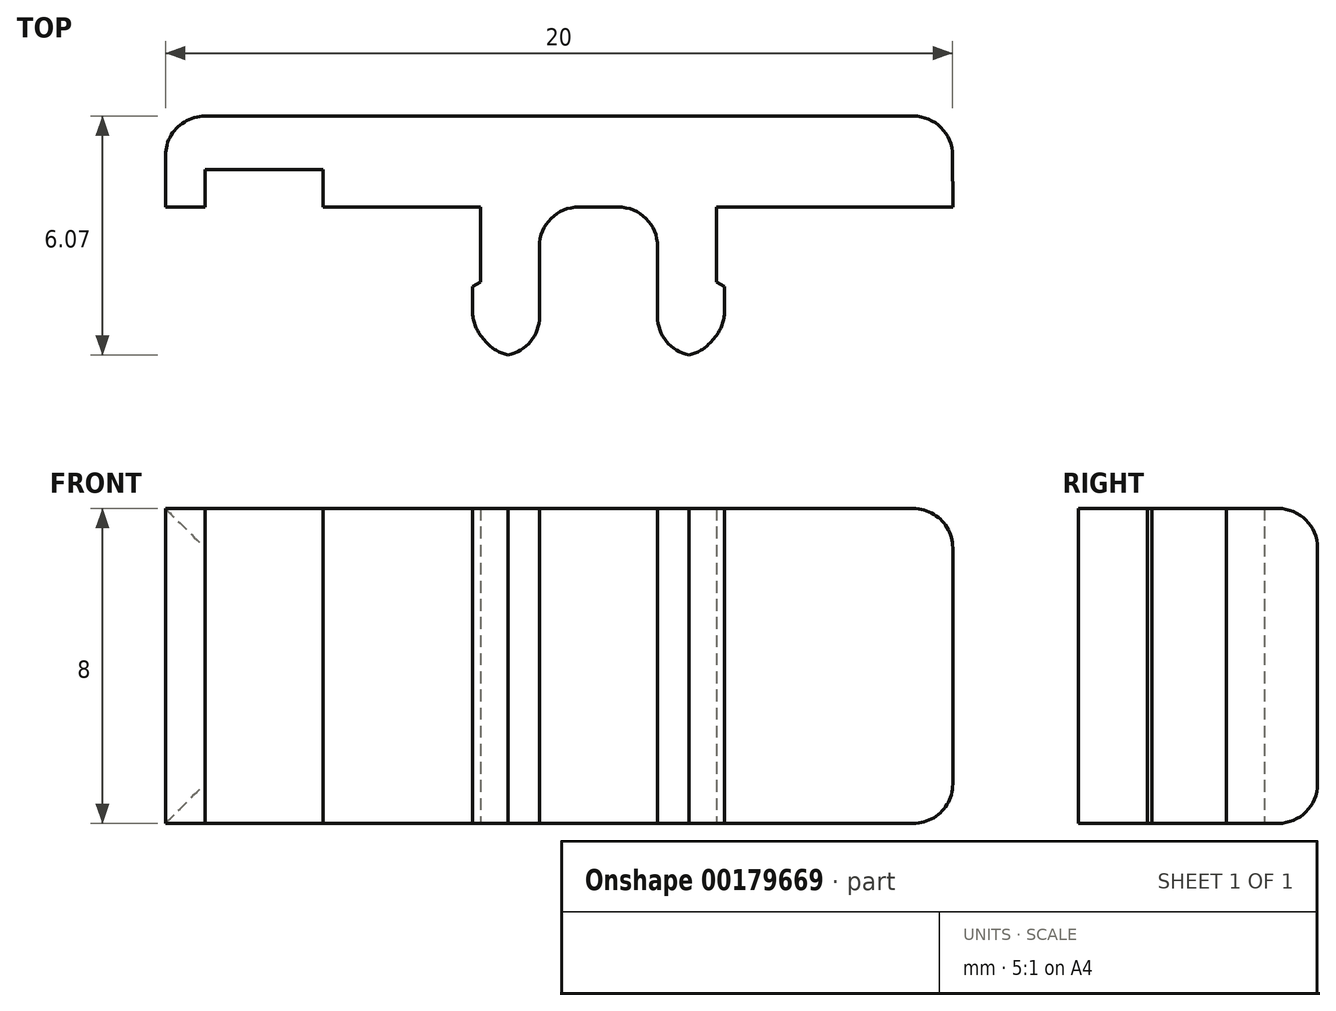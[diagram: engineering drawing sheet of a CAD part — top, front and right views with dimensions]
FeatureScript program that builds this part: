
annotation { "Feature Type Name" : "Feature", "Feature Type Description" : "" }
export const myFeature = defineFeature(function(context is Context, id is Id, definition is map)
    precondition{}
    {
        {
            var Q0;
            Q0=qCreatedBy(makeId("Top.planeOp"),FACE);
            var sketch = newSketch(context, id + "F0", { "sketchPlane" : qUnion([Q0])});
            skLineSegment(sketch, "E0", {"start": v(16.12, 0) * mm, "end": v(10.12, 0) * mm});
            skLineSegment(sketch, "E1", {"start": v(10.12, 0) * mm, "end": v(10.12, -1.9) * mm});
            skLineSegment(sketch, "E2", {"start": v(10.12, -1.9) * mm, "end": v(10.32, -2.02) * mm});
            skLineSegment(sketch, "E3", {"start": v(10.32, -2.02) * mm, "end": v(10.32, -3.02) * mm});
            skLineSegment(sketch, "E4", {"start": v(10.32, -3.02) * mm, "end": v(9.68, -3.78) * mm});
            skLineSegment(sketch, "E5", {"start": v(9.68, -3.78) * mm, "end": v(8.62, -3.78) * mm});
            skLineSegment(sketch, "E6", {"start": v(4.12, 0) * mm, "end": v(0.12, 0) * mm});
            skLineSegment(sketch, "E7", {"start": v(0.12, 0) * mm, "end": v(0.12, 0.95) * mm});
            skLineSegment(sketch, "E8", {"start": v(0.12, 0.95) * mm, "end": v(-2.88, 0.95) * mm});
            skLineSegment(sketch, "E9", {"start": v(-2.88, 0.95) * mm, "end": v(-2.88, 0) * mm});
            skLineSegment(sketch, "E10", {"start": v(-2.88, 0) * mm, "end": v(-3.88, 0) * mm});
            skLineSegment(sketch, "E11", {"start": v(-3.88, 0) * mm, "end": v(-3.88, 2.3) * mm});
            skLineSegment(sketch, "E12", {"start": v(-3.88, 2.3) * mm, "end": v(16.12, 2.3) * mm});
            skLineSegment(sketch, "E13", {"start": v(16.12, 2.3) * mm, "end": v(16.12, 0) * mm});
            skLineSegment(sketch, "E14", {"start": v(7.12, 0) * mm, "end": v(8.62, 0) * mm});
            skLineSegment(sketch, "E15", {"start": v(8.62, 0) * mm, "end": v(8.62, -3.78) * mm});
            skLineSegment(sketch, "E16", {"start": v(7.12, 4.05) * mm, "end": v(7.12, -5.04) * mm, "construction": true});
            skLineSegment(sketch, "E17.MirrorCS", {"start": v(7.12, 0) * mm, "end": v(5.62, 0) * mm});
            skLineSegment(sketch, "E18.MirrorCS", {"start": v(5.62, 0) * mm, "end": v(5.62, -3.78) * mm});
            skLineSegment(sketch, "E19.MirrorCS", {"start": v(4.57, -3.78) * mm, "end": v(5.62, -3.78) * mm});
            skLineSegment(sketch, "E20.MirrorCS", {"start": v(3.92, -3.02) * mm, "end": v(4.57, -3.78) * mm});
            skLineSegment(sketch, "E21.MirrorCS", {"start": v(3.92, -2.02) * mm, "end": v(3.92, -3.02) * mm});
            skLineSegment(sketch, "E22.MirrorCS", {"start": v(4.12, -1.9) * mm, "end": v(3.92, -2.02) * mm});
            skLineSegment(sketch, "E23.MirrorCS", {"start": v(4.12, 0) * mm, "end": v(4.12, -1.9) * mm});
            skSolve(sketch);
        }
        {
            var Q0;
            Q0=qSketchRegion(id+"F0",true);
            extrude(context, id + "F1", {"entities" : qUnion([Q0]), "depth" : 8 * mm});
        }
        {
            var Q0;
            Q0=makeQuery(id+"F1.opExtrude","SWEPT_EDGE",EDGE,{"disambiguationData":[OSD([sQuery(id+"F0.wireOp",EDGE,"E20.MirrorCS"),sQuery(id+"F0.wireOp",EDGE,"E21.MirrorCS")])]});
            var Q1;
            Q1=makeQuery(id+"F1.opExtrude","SWEPT_EDGE",EDGE,{"disambiguationData":[OSD([sQuery(id+"F0.wireOp",EDGE,"E3"),sQuery(id+"F0.wireOp",EDGE,"E4")])]});
            var Q2;
            Q2=makeQuery(id+"F1.opExtrude","SWEPT_EDGE",EDGE,{"disambiguationData":[OSD([sQuery(id+"F0.wireOp",EDGE,"E19.MirrorCS"),sQuery(id+"F0.wireOp",EDGE,"E20.MirrorCS")])]});
            var Q3;
            Q3=makeQuery(id+"F1.opExtrude","SWEPT_EDGE",EDGE,{"disambiguationData":[OSD([sQuery(id+"F0.wireOp",EDGE,"E4"),sQuery(id+"F0.wireOp",EDGE,"E5")])]});
            var Q4;
            Q4=makeQuery(id+"F1.opExtrude","SWEPT_EDGE",EDGE,{"disambiguationData":[OSD([sQuery(id+"F0.wireOp",EDGE,"E5"),sQuery(id+"F0.wireOp",EDGE,"E15")])]});
            var Q5;
            Q5=makeQuery(id+"F1.opExtrude","SWEPT_EDGE",EDGE,{"disambiguationData":[OSD([sQuery(id+"F0.wireOp",EDGE,"E18.MirrorCS"),sQuery(id+"F0.wireOp",EDGE,"E19.MirrorCS")])]});
            var Q6;
            Q6=makeQuery(id+"F1.opExtrude","SWEPT_EDGE",EDGE,{"disambiguationData":[OSD([sQuery(id+"F0.wireOp",EDGE,"E14"),sQuery(id+"F0.wireOp",EDGE,"E15")])]});
            var Q7;
            Q7=makeQuery(id+"F1.opExtrude","SWEPT_EDGE",EDGE,{"disambiguationData":[OSD([sQuery(id+"F0.wireOp",EDGE,"E17.MirrorCS"),sQuery(id+"F0.wireOp",EDGE,"E18.MirrorCS")])]});
            var Q8;
            Q8=makeQuery(id+"F1.opExtrude","SWEPT_FACE",FACE,{"disambiguationData":[OSD([sQuery(id+"F0.wireOp",EDGE,"E12")])]});
            var Q9;
            Q9=makeQuery(id+"F1.opExtrude","CAP_EDGE",EDGE,{"disambiguationData":[OSD([sQuery(id+"F0.wireOp",EDGE,"E13")])],"isStart":false});
            var Q10;
            Q10=makeQuery(id+"F1.opExtrude","CAP_EDGE",EDGE,{"disambiguationData":[OSD([sQuery(id+"F0.wireOp",EDGE,"E13")])],"isStart":true});
            fillet(context, id + "F2", {"entities" : qUnion([Q0, Q1, Q2, Q3, Q4, Q5, Q6, Q7, Q8, Q9, Q10]), "radius" : 1 * mm, "allowEdgeOverflow" : false});
        }
    });
